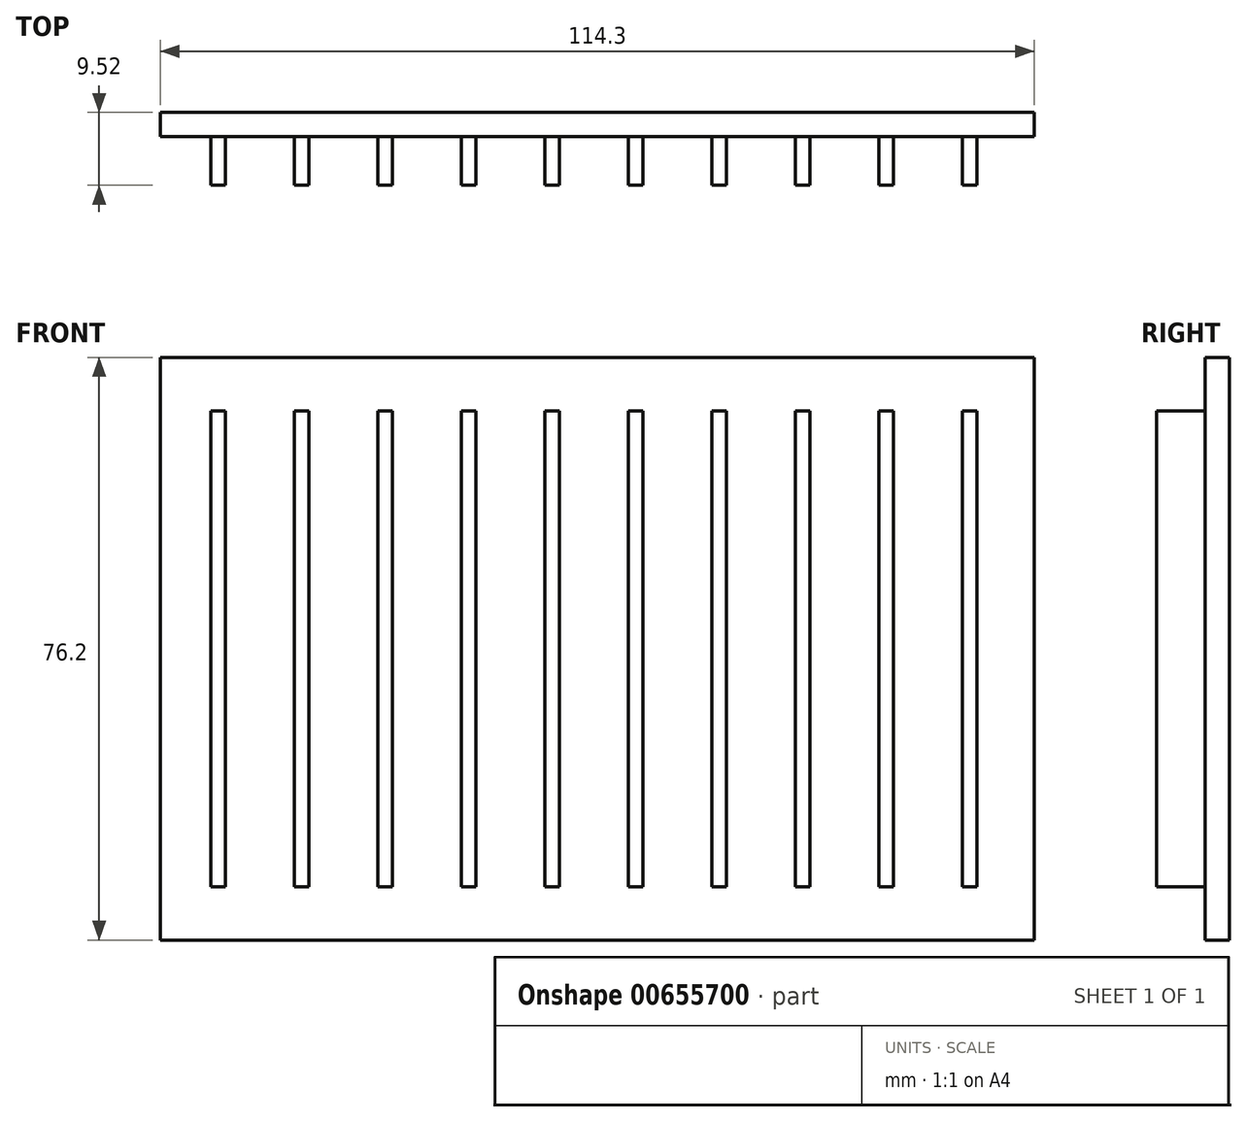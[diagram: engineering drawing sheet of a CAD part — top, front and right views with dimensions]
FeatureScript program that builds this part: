
annotation { "Feature Type Name" : "Feature", "Feature Type Description" : "" }
export const myFeature = defineFeature(function(context is Context, id is Id, definition is map)
    precondition{}
    {
        {
            var Q0;
            Q0=qCreatedBy(makeId("Front.planeOp"),FACE);
            var sketch = newSketch(context, id + "F0", { "sketchPlane" : qUnion([Q0])});
            skLineSegment(sketch, "E0.bottom", {"start": v(57.15, -38.1) * mm, "end": v(-57.15, -38.1) * mm});
            skLineSegment(sketch, "E0.top", {"start": v(57.15, 38.1) * mm, "end": v(-57.15, 38.1) * mm});
            skLineSegment(sketch, "E0.left", {"start": v(57.15, -38.1) * mm, "end": v(57.15, 38.1) * mm});
            skLineSegment(sketch, "E0.right", {"start": v(-57.15, -38.1) * mm, "end": v(-57.15, 38.1) * mm});
            skPoint(sketch, "E0.middle", {"position": v(0, 0) * mm});
            skSolve(sketch);
        }
        {
            var Q0;
            Q0 = qSketchRegion(id + "F0", true);
            extrude(context, id + "F1", {"entities" : qUnion([Q0]), "oppositeDirection" : true, "depth" : 3.17 * mm, "offsetDistance" : 25.4 * mm});
        }
        {
            var Q0;
            Q0=makeQuery(id+"F1.opExtrude","CAP_FACE",FACE,{"disambiguationData":[OSD([sQuery(id+"F0.wireOp",EDGE,"E0.bottom"),sQuery(id+"F0.wireOp",EDGE,"E0.top"),sQuery(id+"F0.wireOp",EDGE,"E0.left"),sQuery(id+"F0.wireOp",EDGE,"E0.right")])],"isStart":true});
            var sketch = newSketch(context, id + "F2", { "sketchPlane" : qUnion([Q0])});
            skLineSegment(sketch, "E1.bottom", {"start": v(-48.66, -31.12) * mm, "end": v(-50.55, -31.12) * mm});
            skLineSegment(sketch, "E1.top", {"start": v(-48.66, 31.12) * mm, "end": v(-50.55, 31.12) * mm});
            skLineSegment(sketch, "E1.left", {"start": v(-48.66, -31.12) * mm, "end": v(-48.66, 31.12) * mm});
            skLineSegment(sketch, "E1.right", {"start": v(-50.55, -31.12) * mm, "end": v(-50.55, 31.12) * mm});
            skPoint(sketch, "E1.middle", {"position": v(-49.6, 0) * mm});
            skLineSegment(sketch, "E2.1.0.0", {"start": v(-37.74, 31.12) * mm, "end": v(-39.62, 31.12) * mm});
            skLineSegment(sketch, "E2.1.0.1", {"start": v(-37.74, -31.12) * mm, "end": v(-37.74, 31.12) * mm});
            skLineSegment(sketch, "E2.1.0.2", {"start": v(-39.62, -31.12) * mm, "end": v(-39.62, 31.12) * mm});
            skLineSegment(sketch, "E2.1.0.3", {"start": v(-37.74, -31.12) * mm, "end": v(-39.62, -31.12) * mm});
            skLineSegment(sketch, "E2.2.0.0", {"start": v(-26.82, 31.12) * mm, "end": v(-28.7, 31.12) * mm});
            skLineSegment(sketch, "E2.2.0.1", {"start": v(-26.82, -31.12) * mm, "end": v(-26.82, 31.12) * mm});
            skLineSegment(sketch, "E2.2.0.2", {"start": v(-28.7, -31.12) * mm, "end": v(-28.7, 31.12) * mm});
            skLineSegment(sketch, "E2.2.0.3", {"start": v(-26.82, -31.12) * mm, "end": v(-28.7, -31.12) * mm});
            skLineSegment(sketch, "E2.3.0.0", {"start": v(-15.9, 31.12) * mm, "end": v(-17.78, 31.12) * mm});
            skLineSegment(sketch, "E2.3.0.1", {"start": v(-15.9, -31.12) * mm, "end": v(-15.9, 31.12) * mm});
            skLineSegment(sketch, "E2.3.0.2", {"start": v(-17.78, -31.12) * mm, "end": v(-17.78, 31.12) * mm});
            skLineSegment(sketch, "E2.3.0.3", {"start": v(-15.9, -31.12) * mm, "end": v(-17.78, -31.12) * mm});
            skLineSegment(sketch, "E2.4.0.0", {"start": v(-4.98, 31.12) * mm, "end": v(-6.86, 31.12) * mm});
            skLineSegment(sketch, "E2.4.0.1", {"start": v(-4.98, -31.11) * mm, "end": v(-4.98, 31.12) * mm});
            skLineSegment(sketch, "E2.4.0.2", {"start": v(-6.86, -31.11) * mm, "end": v(-6.86, 31.12) * mm});
            skLineSegment(sketch, "E2.4.0.3", {"start": v(-4.98, -31.12) * mm, "end": v(-6.86, -31.12) * mm});
            skLineSegment(sketch, "E2.5.0.0", {"start": v(5.95, 31.12) * mm, "end": v(4.06, 31.12) * mm});
            skLineSegment(sketch, "E2.5.0.1", {"start": v(5.95, -31.11) * mm, "end": v(5.95, 31.12) * mm});
            skLineSegment(sketch, "E2.5.0.2", {"start": v(4.06, -31.11) * mm, "end": v(4.06, 31.12) * mm});
            skLineSegment(sketch, "E2.5.0.3", {"start": v(5.95, -31.12) * mm, "end": v(4.06, -31.12) * mm});
            skLineSegment(sketch, "E2.6.0.0", {"start": v(16.87, 31.12) * mm, "end": v(14.99, 31.12) * mm});
            skLineSegment(sketch, "E2.6.0.1", {"start": v(16.87, -31.11) * mm, "end": v(16.87, 31.12) * mm});
            skLineSegment(sketch, "E2.6.0.2", {"start": v(14.99, -31.11) * mm, "end": v(14.99, 31.12) * mm});
            skLineSegment(sketch, "E2.6.0.3", {"start": v(16.87, -31.12) * mm, "end": v(14.99, -31.12) * mm});
            skLineSegment(sketch, "E2.7.0.0", {"start": v(27.79, 31.12) * mm, "end": v(25.9, 31.12) * mm});
            skLineSegment(sketch, "E2.7.0.1", {"start": v(27.79, -31.11) * mm, "end": v(27.79, 31.12) * mm});
            skLineSegment(sketch, "E2.7.0.2", {"start": v(25.9, -31.11) * mm, "end": v(25.9, 31.12) * mm});
            skLineSegment(sketch, "E2.7.0.3", {"start": v(27.79, -31.11) * mm, "end": v(25.9, -31.11) * mm});
            skLineSegment(sketch, "E2.8.0.0", {"start": v(38.71, 31.12) * mm, "end": v(36.83, 31.12) * mm});
            skLineSegment(sketch, "E2.8.0.1", {"start": v(38.71, -31.11) * mm, "end": v(38.71, 31.12) * mm});
            skLineSegment(sketch, "E2.8.0.2", {"start": v(36.83, -31.11) * mm, "end": v(36.83, 31.12) * mm});
            skLineSegment(sketch, "E2.8.0.3", {"start": v(38.71, -31.11) * mm, "end": v(36.83, -31.11) * mm});
            skLineSegment(sketch, "E2.9.0.0", {"start": v(49.63, 31.12) * mm, "end": v(47.75, 31.12) * mm});
            skLineSegment(sketch, "E2.9.0.1", {"start": v(49.63, -31.11) * mm, "end": v(49.63, 31.12) * mm});
            skLineSegment(sketch, "E2.9.0.2", {"start": v(47.75, -31.11) * mm, "end": v(47.75, 31.12) * mm});
            skLineSegment(sketch, "E2.9.0.3", {"start": v(49.63, -31.11) * mm, "end": v(47.75, -31.11) * mm});
            skLineSegment(sketch, "E2.direction1", {"start": v(-50.55, 31.12) * mm, "end": v(-39.62, 31.12) * mm, "construction": true});
            skSolve(sketch);
        }
        {
            var Q0;
            Q0 = qSketchRegion(id + "F2", true);
            extrude(context, id + "F3", {"entities" : qUnion([Q0]), "operationType" : NewBodyOperationType.ADD, "depth" : 6.35 * mm, "offsetDistance" : 25.4 * mm});
        }
    });
